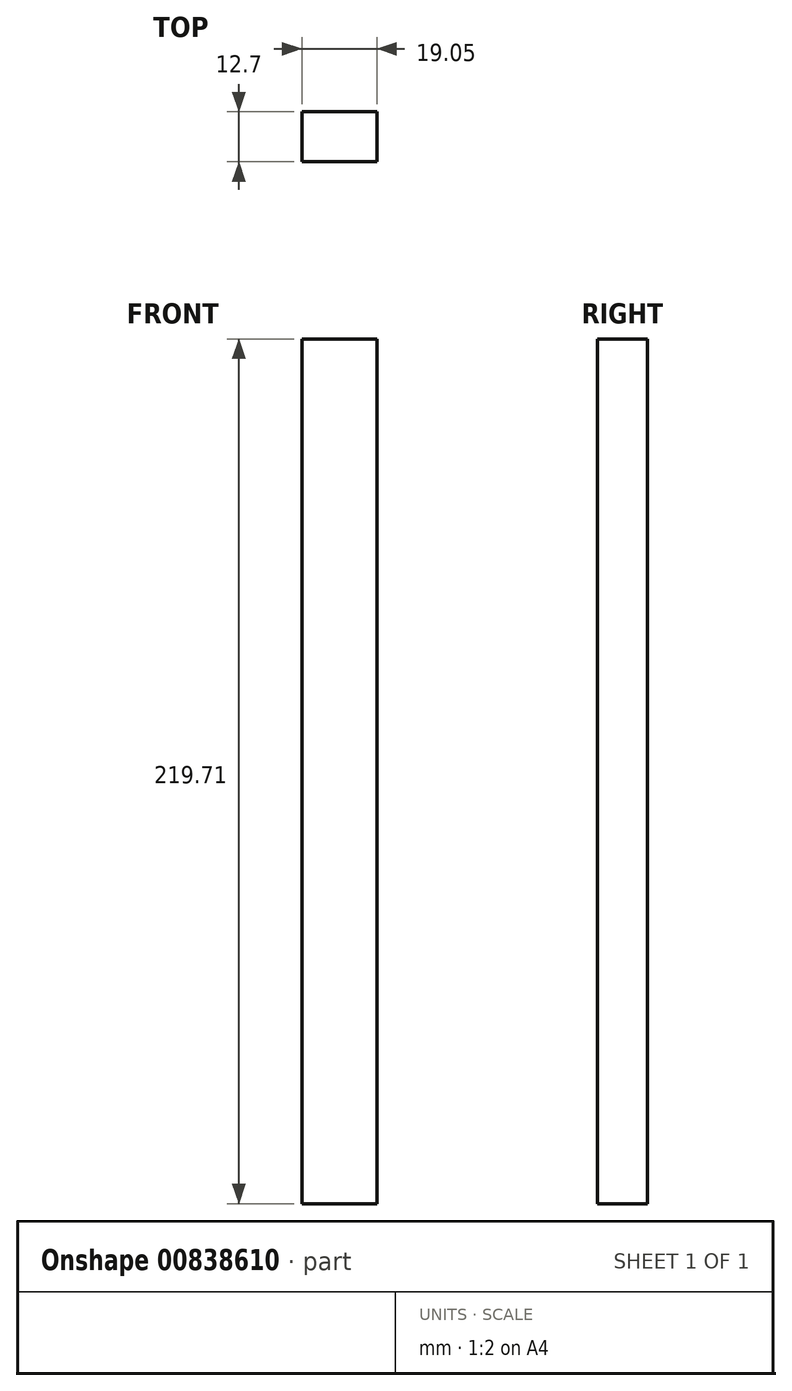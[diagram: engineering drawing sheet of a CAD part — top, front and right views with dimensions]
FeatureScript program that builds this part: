
annotation { "Feature Type Name" : "Feature", "Feature Type Description" : "" }
export const myFeature = defineFeature(function(context is Context, id is Id, definition is map)
    precondition{}
    {
        {
            var Q0;
            Q0=qCreatedBy(makeId("Front.planeOp"),FACE);
            var sketch = newSketch(context, id + "F0", { "sketchPlane" : qUnion([Q0])});
            skLineSegment(sketch, "E0.bottom", {"start": v(-6.26, 139.58) * mm, "end": v(12.8, 139.58) * mm});
            skLineSegment(sketch, "E0.top", {"start": v(-6.26, -80.13) * mm, "end": v(12.8, -80.13) * mm});
            skLineSegment(sketch, "E0.left", {"start": v(-6.26, 139.58) * mm, "end": v(-6.26, -80.13) * mm});
            skLineSegment(sketch, "E0.right", {"start": v(12.8, 139.58) * mm, "end": v(12.8, -80.13) * mm});
            skSolve(sketch);
        }
        {
            var Q0;
            Q0=makeQuery(id+"F0.imprint","IMPRINT",FACE,{"disambiguationData":[TD([[makeQuery(id+"F0.imprint","IMPRINT",EDGE,{"derivedFrom":sQuery(id+"F0.wireOp",EDGE,"E0.bottom")}),-1.0]])]});
            extrude(context, id + "F1", {"entities" : qUnion([Q0]), "depth" : 12.7 * mm, "offsetDistance" : 25.4 * mm});
        }
    });
